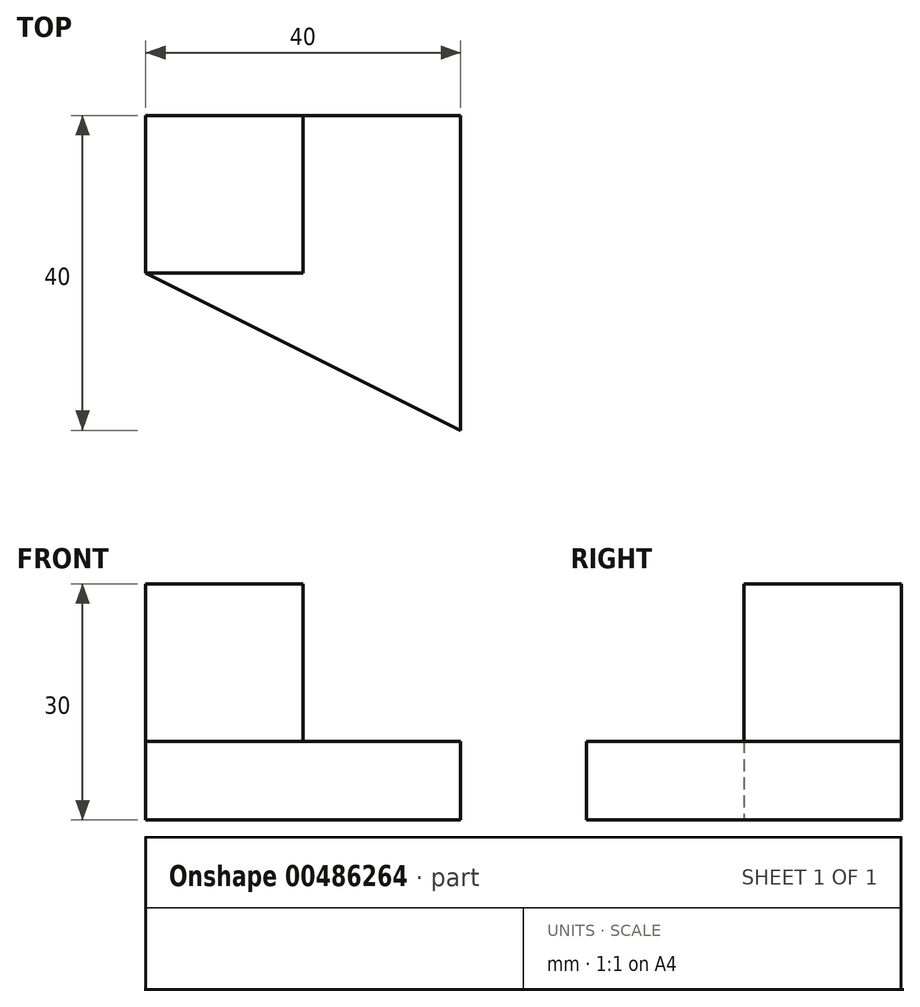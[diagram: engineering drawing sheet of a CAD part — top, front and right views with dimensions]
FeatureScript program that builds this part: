
annotation { "Feature Type Name" : "Feature", "Feature Type Description" : "" }
export const myFeature = defineFeature(function(context is Context, id is Id, definition is map)
    precondition{}
    {
        {
            var Q0;
            Q0=qCreatedBy(makeId("Top.planeOp"),FACE);
            var sketch = newSketch(context, id + "F0", { "sketchPlane" : qUnion([Q0])});
            skLineSegment(sketch, "E0.bottom", {"start": v(-44.67, 61.56) * mm, "end": v(-24.67, 61.56) * mm});
            skLineSegment(sketch, "E0.top", {"start": v(-44.67, 41.56) * mm, "end": v(-24.67, 41.56) * mm});
            skLineSegment(sketch, "E0.left", {"start": v(-44.67, 61.56) * mm, "end": v(-44.67, 41.56) * mm});
            skLineSegment(sketch, "E0.right", {"start": v(-24.67, 61.56) * mm, "end": v(-24.67, 41.56) * mm});
            skLineSegment(sketch, "E1.bottom", {"start": v(-44.67, 61.56) * mm, "end": v(-4.67, 61.56) * mm});
            skLineSegment(sketch, "E1.right", {"start": v(-4.67, 61.56) * mm, "end": v(-4.67, 21.56) * mm});
            skLineSegment(sketch, "E2", {"start": v(-44.67, 41.56) * mm, "end": v(-4.67, 21.56) * mm});
            skSolve(sketch);
        }
        {
            var Q0;
            Q0=makeQuery(id+"F0.imprint","IMPRINT",FACE,{"disambiguationData":[TD([[makeQuery(id+"F0.imprint","IMPRINT",EDGE,{"derivedFrom":sQuery(id+"F0.wireOp",EDGE,"E0.top")}),1.0]])]});
            var Q1;
            Q1=makeQuery(id+"F0.imprint","IMPRINT",FACE,{"disambiguationData":[TD([[makeQuery(id+"F0.imprint","IMPRINT",EDGE,{"derivedFrom":sQuery(id+"F0.wireOp",EDGE,"E0.top")}),-1.0]])]});
            extrude(context, id + "F1", {"entities" : qUnion([Q0, Q1]), "depth" : 10 * mm});
        }
        {
            var Q0;
            Q0=makeQuery(id+"F0.imprint","IMPRINT",FACE,{"disambiguationData":[TD([[makeQuery(id+"F0.imprint","IMPRINT",EDGE,{"derivedFrom":sQuery(id+"F0.wireOp",EDGE,"E0.top")}),1.0]])]});
            extrude(context, id + "F2", {"entities" : qUnion([Q0]), "operationType" : NewBodyOperationType.ADD, "depth" : 30 * mm});
        }
    });
